AUTODESK INVENTOR PART (.ipt)
format: ipt  version: 2019 (Build 230136000, 136)  size: 10,073,600 bytes
history: native  units: in
note: dims shown in document units (in); Inventor stores cm internally (conversion verified against a paired STEP export)
features: other x11, direct_edit x5, plane x5, sketch x3, projected_geometry x3, extrude x2, surface_op x1
ambient origin geometry x8: Origin, YZ Plane, XZ Plane, XY Plane, X Axis, Y Axis, Z Axis, Center Point
bodies: Solid1 (feature_tree)
feature tree (30):
  other  "upper_plate"
  surface_op  "Stitch Surface1"
  direct_edit  "Direct Edit1"
  direct_edit  "Direct Edit2"
  direct_edit  "Direct Edit3"
  direct_edit  "Direct Edit4"
  direct_edit  "Direct Edit5"
  plane  "Work Plane1"
  plane  "Work Plane3"
  plane  "Work Plane5"
  other  "Work Axis4"
  other  "Work Axis5"
  plane  "Work Plane8"
  other  "Work Axis7"
  extrude  "Extrusion1"  Depth=0.3937in
  extrude  "Extrusion3"  Depth=0.3937in
  sketch  "Sketch3"  dims[d12=0.3953in d13=0.3937in d14=0.3937in d15=90.0deg d17=90.0deg d18=1.2598in d19=1.2598in d20=1.2598in d21=0.3937in d22=0.0in d23=0.1339in d24=0.1339in d25=0.1339in d26=0.1339in d29=0.3937in d30=0.0in d31=0.1339in]
  plane  "Work Plane9"
  sketch  "Sketch1"  dims[d0=0.0394in d1=0.3937in d2=0.3937in d3=0.1969in d4=0.3937in d5=0.3937in]
  projected_geometry  "Projected Loop1"
  sketch  "Sketch2"  dims[d6=0.2756in d7=0.3937in d8=0.3937in d9=0.4409in d10=0.3937in d11=0.3937in]
  projected_geometry  "Projected Loop2"
  projected_geometry  "Projected Loop3"
  other  "Composite1"
  other  "Srf1"
  other  "Scale1"
  other  "Scale2"
  other  "Scale3"
  other  "Scale4"
  other  "Scale5"
